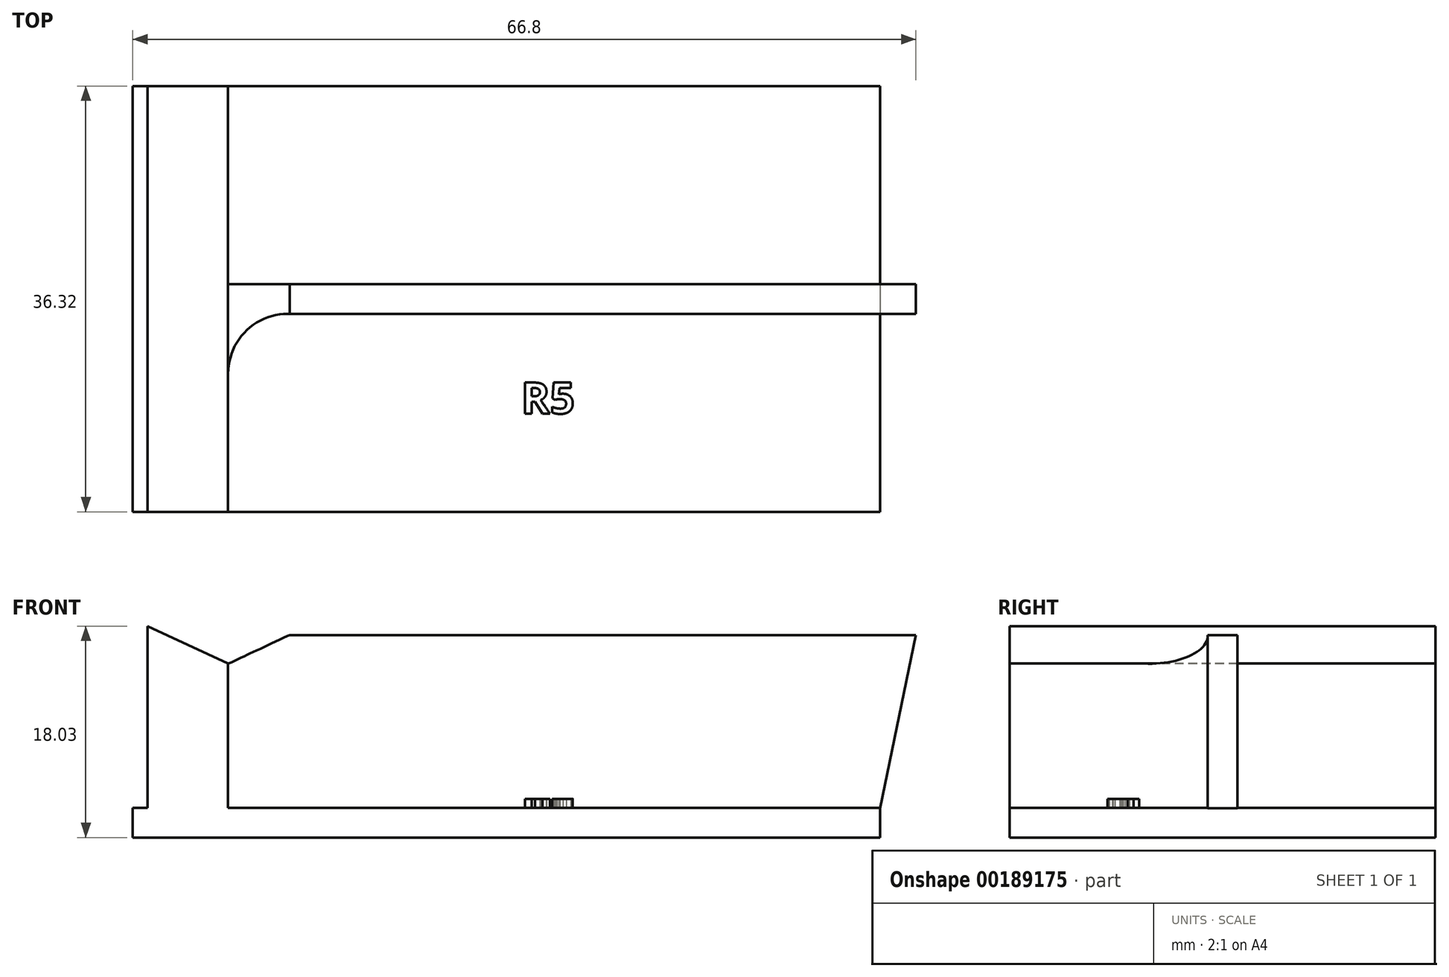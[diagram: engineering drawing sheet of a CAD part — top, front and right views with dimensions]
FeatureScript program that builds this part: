
annotation { "Feature Type Name" : "Feature", "Feature Type Description" : "" }
export const myFeature = defineFeature(function(context is Context, id is Id, definition is map)
    precondition{}
    {
        {
            var Q0;
            Q0=qCreatedBy(makeId("Front.planeOp"),FACE);
            var sketch = newSketch(context, id + "F0", { "sketchPlane" : qUnion([Q0])});
            skLineSegment(sketch, "E0.bottom", {"start": v(0, 0) * mm, "end": v(63.75, 0) * mm});
            skLineSegment(sketch, "E0.top", {"start": v(0, 2.54) * mm, "end": v(63.75, 2.54) * mm});
            skLineSegment(sketch, "E0.left", {"start": v(0, 0) * mm, "end": v(0, 2.54) * mm});
            skLineSegment(sketch, "E0.right", {"start": v(63.75, 0) * mm, "end": v(63.75, 2.54) * mm});
            skLineSegment(sketch, "E1.bottom", {"start": v(0, 2.54) * mm, "end": v(1.27, 2.54) * mm});
            skLineSegment(sketch, "E1.top", {"start": v(0, 18.03) * mm, "end": v(1.27, 18.03) * mm});
            skLineSegment(sketch, "E1.left", {"start": v(0, 2.54) * mm, "end": v(0, 18.03) * mm});
            skLineSegment(sketch, "E1.right", {"start": v(1.27, 2.54) * mm, "end": v(1.27, 18.03) * mm});
            skSolve(sketch);
        }
        {
            var Q0;
            Q0=makeQuery(id+"F0.imprint","IMPRINT",FACE,{"disambiguationData":[TD([[makeQuery(id+"F0.imprint","IMPRINT",EDGE,{"derivedFrom":sQuery(id+"F0.wireOp",EDGE,"E0.bottom")}),1.0]])]});
            var Q1;
            {var subQ1=sQuery(id+"F0.wireOp",EDGE,"E1.bottom");Q1=makeQuery(id+"F0.imprint","IMPRINT",FACE,{"disambiguationData":[TD([[makeQuery(id+"F0.imprint","IMPRINT",EDGE,{"derivedFrom":subQ1}),1.0]])]});}
            extrude(context, id + "F1", {"entities" : qUnion([Q0, Q1]), "oppositeDirection" : true, "depth" : 36.32 * mm});
        }
        {
            var Q0;
            Q0=makeQuery(id+"F1.opExtrude","SWEPT_FACE",FACE,{"disambiguationData":[OSD([sQuery(id+"F0.wireOp",EDGE,"E0.top")])]});
            var sketch = newSketch(context, id + "F2", { "sketchPlane" : qUnion([Q0])});
            skSolve(sketch);
        }
        {
            var Q0;
            Q0=makeQuery(id+"F1.opExtrude","CAP_FACE",FACE,{"disambiguationData":[OSD([sQuery(id+"F0.wireOp",EDGE,"E0.bottom"),sQuery(id+"F0.wireOp",EDGE,"E0.top"),sQuery(id+"F0.wireOp",EDGE,"E0.left"),sQuery(id+"F0.wireOp",EDGE,"E0.right"),sQuery(id+"F0.wireOp",EDGE,"E1.top"),sQuery(id+"F0.wireOp",EDGE,"E1.left"),sQuery(id+"F0.wireOp",EDGE,"E1.right")])],"isStart":true});
            var sketch = newSketch(context, id + "F3", { "sketchPlane" : qUnion([Q0])});
            skLineSegment(sketch, "E2", {"start": v(1.27, 18.03) * mm, "end": v(8.13, 14.84) * mm});
            skLineSegment(sketch, "E3", {"start": v(8.13, 14.84) * mm, "end": v(8.13, 2.54) * mm});
            skLineSegment(sketch, "E4", {"start": v(8.13, 2.54) * mm, "end": v(1.27, 2.54) * mm});
            skLineSegment(sketch, "E5", {"start": v(1.27, 2.54) * mm, "end": v(1.27, 18.03) * mm});
            skSolve(sketch);
        }
        {
            var Q0;
            Q0=qSketchRegion(id+"F3",true);
            extrude(context, id + "F4", {"entities" : qUnion([Q0]), "operationType" : NewBodyOperationType.ADD, "oppositeDirection" : true, "depth" : 36.32 * mm});
        }
        {
            var Q0;
            {var subQ0=sQuery(id+"F0.wireOp",EDGE,"E0.top");Q0=makeQuery(id+"F2.imprint","IMPRINT",FACE,{"disambiguationData":[TD([[makeQuery(id+"F2.imprint","IMPRINT",EDGE,{"derivedFrom":makeQuery(id+"F1.opExtrude","CAP_EDGE",EDGE,{"disambiguationData":[OSD([subQ0])],"isStart":true})}),1.0]])]});}
            var sketch = newSketch(context, id + "F5", { "sketchPlane" : qUnion([Q0])});
            skLineSegment(sketch, "E6", {"start": v(8.13, 18.16) * mm, "end": v(62.47, 18.16) * mm, "construction": true});
            skLineSegment(sketch, "E7.bottom", {"start": v(63.75, 19.43) * mm, "end": v(8.13, 19.43) * mm});
            skLineSegment(sketch, "E7.top", {"start": v(63.75, 16.9) * mm, "end": v(8.13, 16.9) * mm});
            skLineSegment(sketch, "E7.left", {"start": v(63.75, 19.43) * mm, "end": v(63.75, 16.9) * mm});
            skLineSegment(sketch, "E7.right", {"start": v(8.13, 19.43) * mm, "end": v(8.13, 16.9) * mm});
            skSolve(sketch);
        }
        {
            var Q0;
            Q0 = qSketchRegion(id + "F5", true);
            extrude(context, id + "F6", {"entities" : qUnion([Q0]), "operationType" : NewBodyOperationType.ADD, "depth" : 14.73 * mm});
        }
        {
            var Q0;
            Q0=makeQuery(id+"F6.opExtrude","SWEPT_FACE",FACE,{"disambiguationData":[OSD([sQuery(id+"F5.wireOp",EDGE,"E7.top")])]});
            var sketch = newSketch(context, id + "F7", { "sketchPlane" : qUnion([Q0])});
            skSolve(sketch);
        }
        {
            var Q0;
            {var subQ0=sQuery(id+"F5.wireOp",EDGE,"E7.top");Q0=makeQuery(id+"F7.imprint","IMPRINT",FACE,{"disambiguationData":[TD([[makeQuery(id+"F7.imprint","IMPRINT",EDGE,{"derivedFrom":makeQuery(id+"F6.opExtrude","CAP_EDGE",EDGE,{"disambiguationData":[OSD([subQ0])],"isStart":false})}),1.0]])]});}
            var sketch = newSketch(context, id + "F8", { "sketchPlane" : qUnion([Q0])});
            skLineSegment(sketch, "E8", {"start": v(8.13, 14.81) * mm, "end": v(13.37, 17.27) * mm});
            skLineSegment(sketch, "E9", {"start": v(13.37, 17.27) * mm, "end": v(8.13, 17.27) * mm});
            skLineSegment(sketch, "E10", {"start": v(8.13, 17.27) * mm, "end": v(8.13, 14.81) * mm});
            skSolve(sketch);
        }
        {
            var Q0;
            Q0 = qSketchRegion(id + "F8", true);
            extrude(context, id + "F9", {"entities" : qUnion([Q0]), "operationType" : NewBodyOperationType.REMOVE, "oppositeDirection" : true, "depth" : 2.54 * mm});
        }
        {
            var Q0;
            {var subQ0=sQuery(id+"F5.wireOp",EDGE,"E7.top");Q0=makeQuery(id+"F7.imprint","IMPRINT",FACE,{"disambiguationData":[TD([[makeQuery(id+"F7.imprint","IMPRINT",EDGE,{"derivedFrom":makeQuery(id+"F6.opExtrude","CAP_EDGE",EDGE,{"disambiguationData":[OSD([subQ0])],"isStart":false})}),1.0]])]});}
            var sketch = newSketch(context, id + "F10", { "sketchPlane" : qUnion([Q0])});
            skLineSegment(sketch, "E11", {"start": v(63.75, 2.51) * mm, "end": v(63.75, 17.27) * mm});
            skLineSegment(sketch, "E12", {"start": v(63.75, 17.27) * mm, "end": v(66.8, 17.27) * mm});
            skLineSegment(sketch, "E13", {"start": v(66.8, 17.27) * mm, "end": v(63.75, 2.51) * mm});
            skSolve(sketch);
        }
        {
            var Q0;
            Q0 = qSketchRegion(id + "F10", true);
            extrude(context, id + "F11", {"entities" : qUnion([Q0]), "operationType" : NewBodyOperationType.ADD, "oppositeDirection" : true, "depth" : 2.54 * mm});
        }
        {
            var Q0;
            {var subQ0=sQuery(id+"F0.wireOp",EDGE,"E0.top");Q0=makeQuery(id+"F2.imprint","IMPRINT",FACE,{"disambiguationData":[TD([[makeQuery(id+"F2.imprint","IMPRINT",EDGE,{"derivedFrom":makeQuery(id+"F1.opExtrude","CAP_EDGE",EDGE,{"disambiguationData":[OSD([subQ0])],"isStart":true})}),1.0]])]});}
            var sketch = newSketch(context, id + "F12", { "sketchPlane" : qUnion([Q0])});
            skText(sketch, "E14", { "text": "R5", "fontName": "OpenSans-Bold.ttf"});
            const initialGuessF12  = {"E14": [0.03313, 0.00838, 1, 0, 0.00267]};
            skSetInitialGuess(sketch, initialGuessF12);
            skSolve(sketch);
        }
        {
            var Q0;
            Q0 = qSketchRegion(id + "F12", true);
            extrude(context, id + "F13", {"entities" : qUnion([Q0]), "operationType" : NewBodyOperationType.ADD, "depth" : 0.76 * mm});
        }
        {
            var Q0;
            {var subQ0=sQuery(id+"F5.wireOp",EDGE,"E7.top");var subQ1=sQuery(id+"F5.wireOp",EDGE,"E7.right");Q0=makeQuery(id+"F6.boolean.opBoolean","SPLIT",EDGE,{"disambiguationData":[TD([makeQuery(id+"F1.opExtrude","SWEPT_FACE",FACE,{"disambiguationData":[OSD([sQuery(id+"F0.wireOp",EDGE,"E0.top")])]})])],"derivedFrom":makeQuery(id+"F6.opExtrude","SWEPT_EDGE",EDGE,{"disambiguationData":[OSD([subQ0,subQ1])]})});}
            var Q1;
            {var subQ0=sQuery(id+"F5.wireOp",EDGE,"E7.bottom");var subQ1=sQuery(id+"F5.wireOp",EDGE,"E7.right");Q1=makeQuery(id+"F6.boolean.opBoolean","SPLIT",EDGE,{"disambiguationData":[TD([makeQuery(id+"F1.opExtrude","SWEPT_FACE",FACE,{"disambiguationData":[OSD([sQuery(id+"F0.wireOp",EDGE,"E0.top")])]})])],"derivedFrom":makeQuery(id+"F6.opExtrude","SWEPT_EDGE",EDGE,{"disambiguationData":[OSD([subQ0,subQ1])]})});}
            fillet(context, id + "F14", {"entities" : qUnion([Q0, Q1]), "radius" : 5.08 * mm, "tangentPropagation" : true, "allowEdgeOverflow" : false});
        }
    });
